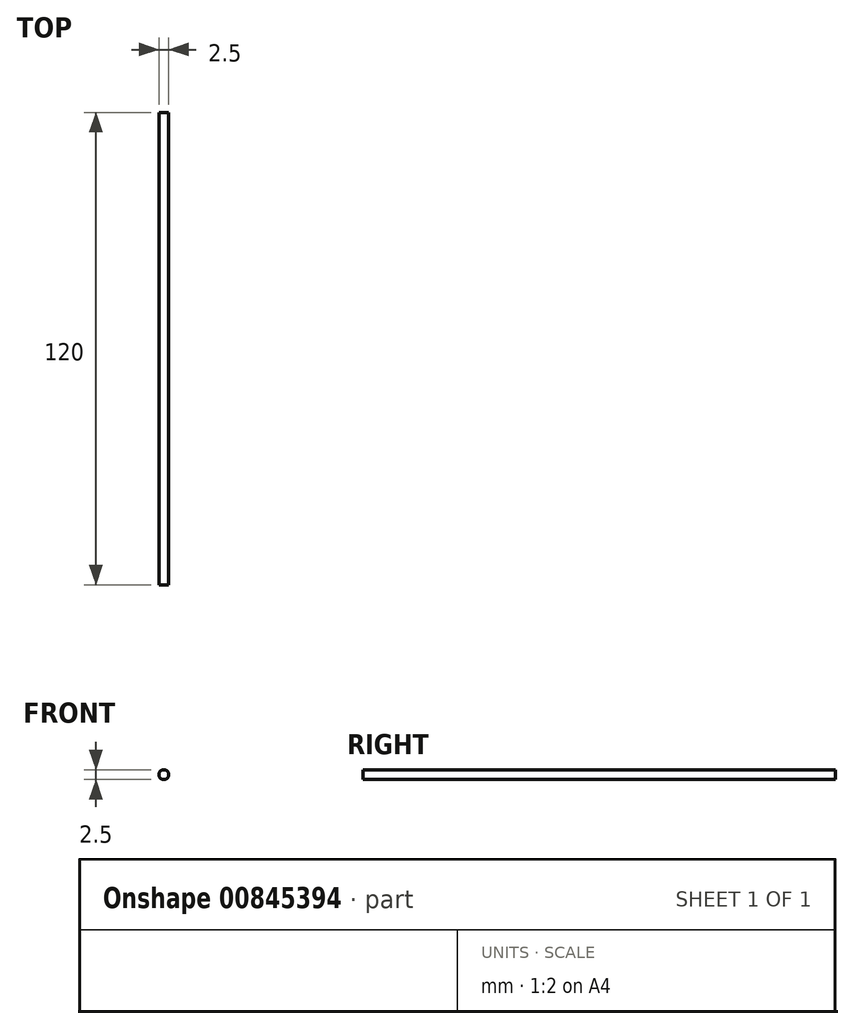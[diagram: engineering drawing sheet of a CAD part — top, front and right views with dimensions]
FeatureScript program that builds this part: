
annotation { "Feature Type Name" : "Feature", "Feature Type Description" : "" }
export const myFeature = defineFeature(function(context is Context, id is Id, definition is map)
    precondition{}
    {
        {
            var Q0;
            Q0=qCreatedBy(makeId("Front.planeOp"),FACE);
            var sketch = newSketch(context, id + "F0", { "sketchPlane" : qUnion([Q0])});
            skCircle(sketch, "E0", {"center": v(0, 0) * mm, "radius": 1.25 * mm});
            skSolve(sketch);
        }
        {
            var Q0;
            Q0=makeQuery(id+"F0.imprint","IMPRINT",FACE,{"disambiguationData":[TD([[makeQuery(id+"F0.imprint","IMPRINT",EDGE,{"derivedFrom":sQuery(id+"F0.wireOp",EDGE,"E0")}),1.0]])]});
            extrude(context, id + "F1", {"entities" : qUnion([Q0]), "depth" : 120 * mm, "offsetDistance" : 25 * mm});
        }
    });
